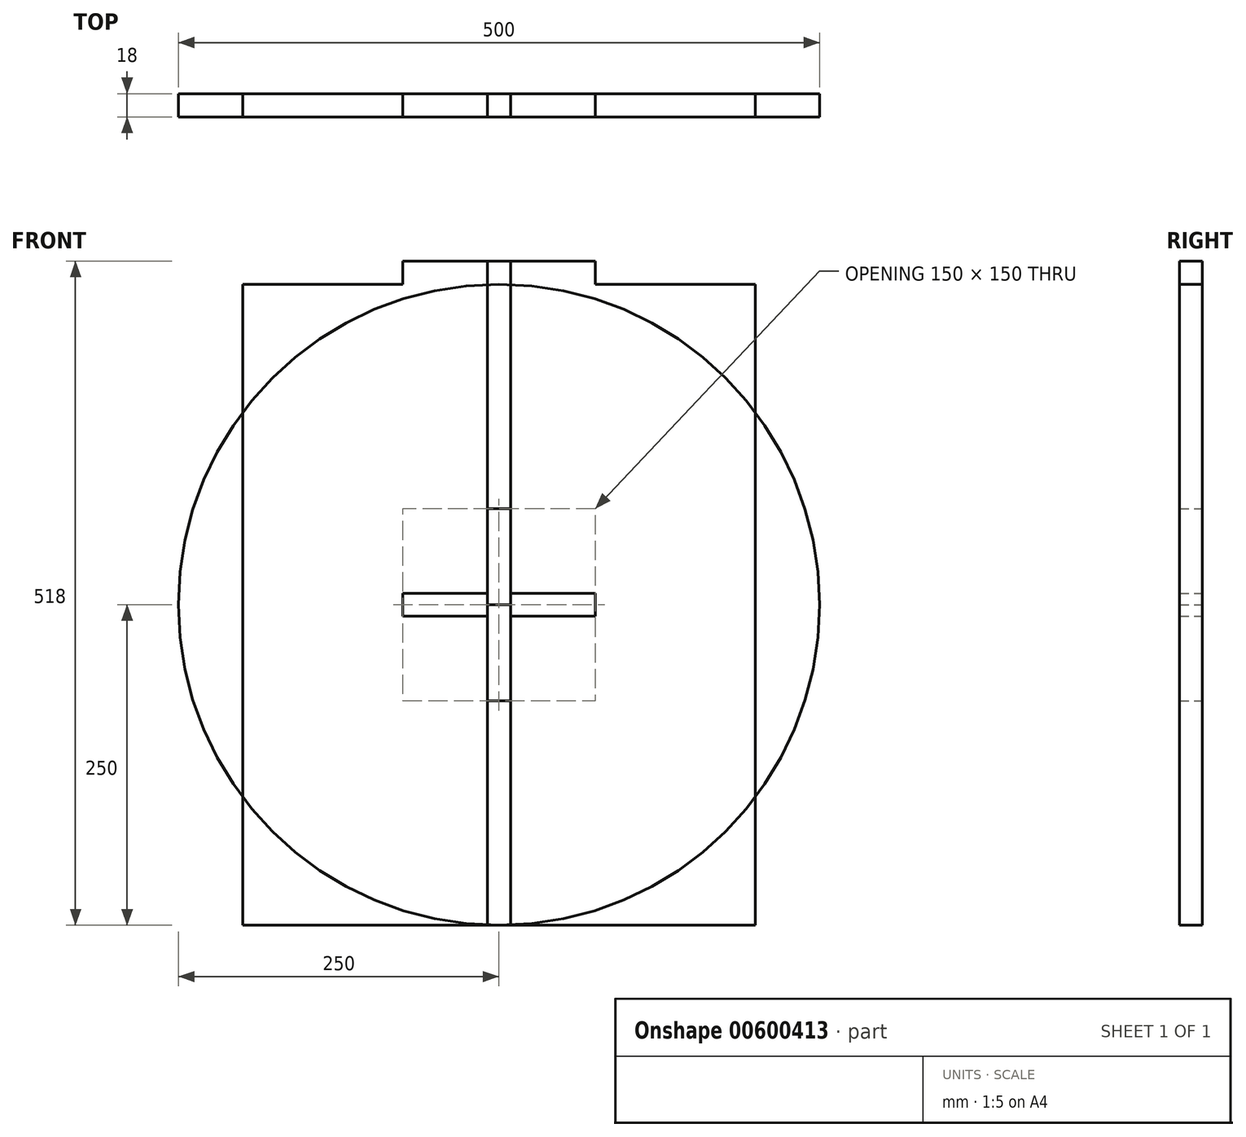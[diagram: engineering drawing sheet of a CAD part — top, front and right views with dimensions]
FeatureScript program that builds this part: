
annotation { "Feature Type Name" : "Feature", "Feature Type Description" : "" }
export const myFeature = defineFeature(function(context is Context, id is Id, definition is map)
    precondition{}
    {
        {
            var Q0;
            Q0=qCreatedBy(makeId("Front.planeOp"),FACE);
            var sketch = newSketch(context, id + "F0", { "sketchPlane" : qUnion([Q0])});
            skLineSegment(sketch, "E0.bottom", {"start": v(200, -250) * mm, "end": v(-200, -250) * mm});
            skLineSegment(sketch, "E0.top", {"start": v(200, 250) * mm, "end": v(75, 250) * mm});
            skLineSegment(sketch, "E0.left", {"start": v(200, -250) * mm, "end": v(200, 250) * mm});
            skLineSegment(sketch, "E0.right", {"start": v(-200, -250) * mm, "end": v(-200, 250) * mm});
            skPoint(sketch, "E0.middle", {"position": v(0, 0) * mm});
            skLineSegment(sketch, "E1.top", {"start": v(75, 268) * mm, "end": v(9, 268) * mm});
            skLineSegment(sketch, "E2.trimOffspring", {"start": v(-75, 250) * mm, "end": v(-200, 250) * mm});
            skLineSegment(sketch, "E3.trimOffspring", {"start": v(75, 250) * mm, "end": v(75, 268) * mm});
            skLineSegment(sketch, "E4.trimOffspring", {"start": v(-75, 250) * mm, "end": v(-75, 268) * mm});
            skLineSegment(sketch, "E5.left", {"start": v(9, 268) * mm, "end": v(9, 0) * mm});
            skLineSegment(sketch, "E5.right", {"start": v(-9, 268) * mm, "end": v(-9, 0) * mm});
            skLineSegment(sketch, "E6.trimOffspring", {"start": v(-9, 268) * mm, "end": v(-75, 268) * mm});
            skLineSegment(sketch, "E7", {"start": v(9, 0) * mm, "end": v(-9, 0) * mm});
            skSolve(sketch);
        }
        {
            var Q0;
            Q0=qCreatedBy(makeId("Front.planeOp"),FACE);
            var sketch = newSketch(context, id + "F1", { "sketchPlane" : qUnion([Q0])});
            skLineSegment(sketch, "E8.bottom", {"start": v(200, -250) * mm, "end": v(9, -250) * mm});
            skLineSegment(sketch, "E8.top", {"start": v(200, 250) * mm, "end": v(75, 250) * mm});
            skLineSegment(sketch, "E8.left", {"start": v(200, -250) * mm, "end": v(200, 250) * mm});
            skLineSegment(sketch, "E8.right", {"start": v(-200, -250) * mm, "end": v(-200, 250) * mm});
            skPoint(sketch, "E8.middle", {"position": v(0, 0) * mm});
            skLineSegment(sketch, "E9.top", {"start": v(75, 268) * mm, "end": v(-75, 268) * mm});
            skLineSegment(sketch, "E10.trimOffspring", {"start": v(-75, 250) * mm, "end": v(-200, 250) * mm});
            skLineSegment(sketch, "E11.trimOffspring", {"start": v(75, 250) * mm, "end": v(75, 268) * mm});
            skLineSegment(sketch, "E12.trimOffspring", {"start": v(-75, 250) * mm, "end": v(-75, 268) * mm});
            skLineSegment(sketch, "E13", {"start": v(200, -250) * mm, "end": v(200, 0) * mm, "construction": true});
            skLineSegment(sketch, "E14", {"start": v(200, 0) * mm, "end": v(-200, 0) * mm, "construction": true});
            skLineSegment(sketch, "E15.left", {"start": v(9, -250) * mm, "end": v(9, 0) * mm});
            skLineSegment(sketch, "E15.right", {"start": v(-9, -250) * mm, "end": v(-9, 0) * mm});
            skLineSegment(sketch, "E16", {"start": v(-9, 0) * mm, "end": v(9, 0) * mm});
            skLineSegment(sketch, "E17.trimOffspring", {"start": v(-9, -250) * mm, "end": v(-200, -250) * mm});
            skSolve(sketch);
        }
        {
            var Q0;
            Q0=qCreatedBy(makeId("Front.planeOp"),FACE);
            var sketch = newSketch(context, id + "F2", { "sketchPlane" : qUnion([Q0])});
            skCircle(sketch, "E18", {"center": v(0, 0) * mm, "radius": 250 * mm});
            skLineSegment(sketch, "E19", {"start": v(0, 0) * mm, "end": v(250, 0) * mm, "construction": true});
            skLineSegment(sketch, "E20", {"start": v(0, 0) * mm, "end": v(0, 250) * mm, "construction": true});
            skLineSegment(sketch, "E21.bottom", {"start": v(75, -9) * mm, "end": v(9, -9) * mm});
            skLineSegment(sketch, "E21.top", {"start": v(75, 9) * mm, "end": v(9, 9) * mm});
            skLineSegment(sketch, "E21.left", {"start": v(75, -9) * mm, "end": v(75, 9) * mm});
            skLineSegment(sketch, "E21.right", {"start": v(-75, -9) * mm, "end": v(-75, 9) * mm});
            skLineSegment(sketch, "E22.bottom", {"start": v(9, -75) * mm, "end": v(-9, -75) * mm});
            skLineSegment(sketch, "E22.top", {"start": v(9, 75) * mm, "end": v(-9, 75) * mm});
            skLineSegment(sketch, "E22.left", {"start": v(9, -75) * mm, "end": v(9, -9) * mm});
            skLineSegment(sketch, "E22.right", {"start": v(-9, -75) * mm, "end": v(-9, -9) * mm});
            skLineSegment(sketch, "E23.trimOffspring", {"start": v(-9, 9) * mm, "end": v(-75, 9) * mm});
            skLineSegment(sketch, "E24.trimOffspring", {"start": v(9, 9) * mm, "end": v(9, 75) * mm});
            skLineSegment(sketch, "E25.trimOffspring", {"start": v(-9, 9) * mm, "end": v(-9, 75) * mm});
            skLineSegment(sketch, "E26.trimOffspring", {"start": v(-9, -9) * mm, "end": v(-75, -9) * mm});
            skSolve(sketch);
        }
        {
            var Q0;
            Q0 = qSketchRegion(id + "F0", true);
            extrude(context, id + "F3", {"entities" : qUnion([Q0]), "depth" : 18 * mm, "offsetDistance" : 25 * mm});
        }
        {
            var Q0;
            Q0 = qSketchRegion(id + "F1", true);
            extrude(context, id + "F4", {"entities" : qUnion([Q0]), "depth" : 18 * mm, "offsetDistance" : 25 * mm});
        }
        {
            var Q0;
            Q0 = qSketchRegion(id + "F2", true);
            extrude(context, id + "F5", {"entities" : qUnion([Q0]), "depth" : 18 * mm, "offsetDistance" : 25 * mm});
        }
    });
